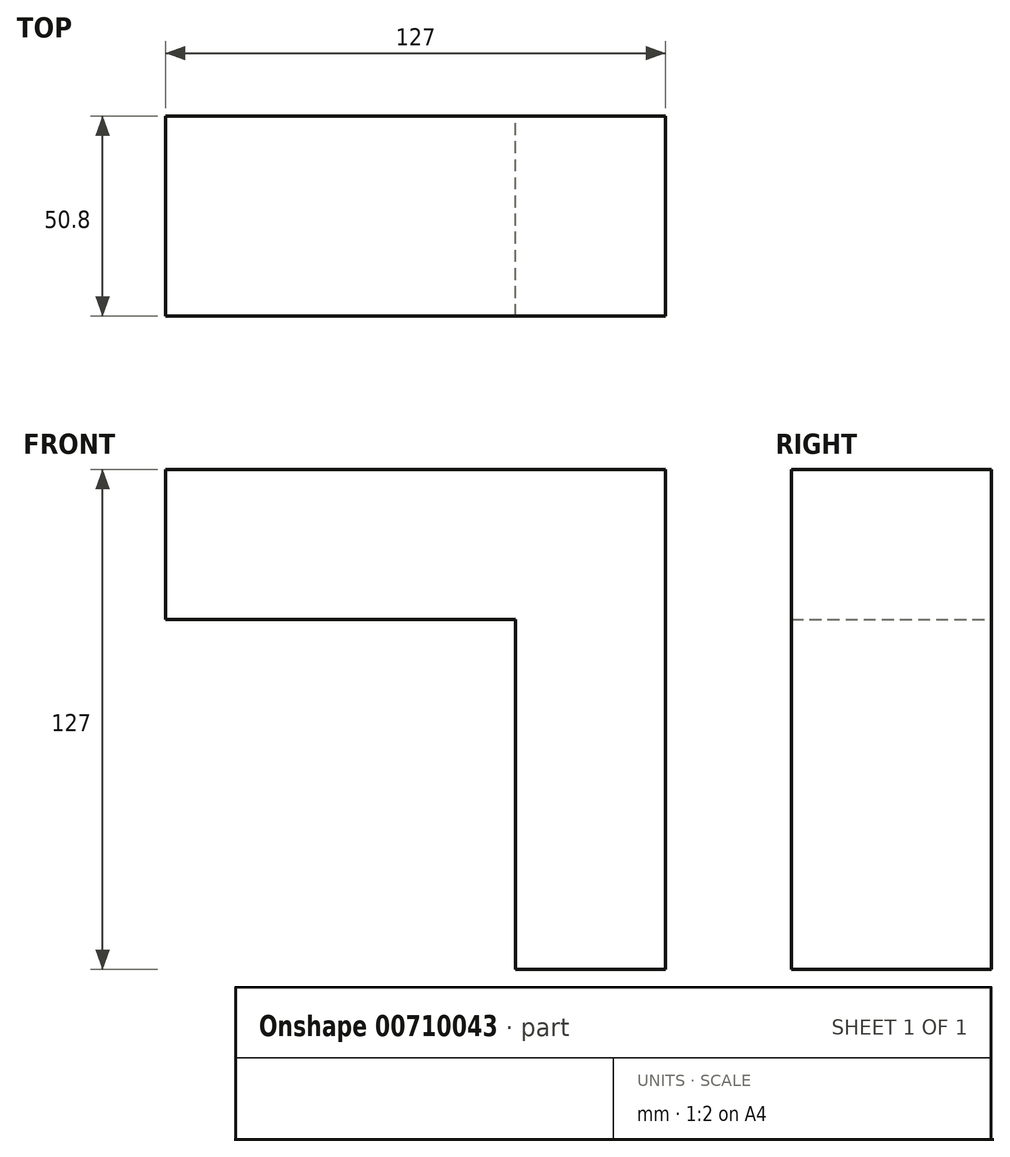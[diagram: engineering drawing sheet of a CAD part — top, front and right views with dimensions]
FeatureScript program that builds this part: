
annotation { "Feature Type Name" : "Feature", "Feature Type Description" : "" }
export const myFeature = defineFeature(function(context is Context, id is Id, definition is map)
    precondition{}
    {
        {
            var Q0;
            Q0=qCreatedBy(makeId("Front.planeOp"),FACE);
            var sketch = newSketch(context, id + "F0", { "sketchPlane" : qUnion([Q0])});
            skLineSegment(sketch, "E0", {"start": v(0, 0) * mm, "end": v(192.92, 0) * mm, "construction": true});
            skLineSegment(sketch, "E1", {"start": v(127, 0) * mm, "end": v(127, 127) * mm});
            skLineSegment(sketch, "E2", {"start": v(127, 127) * mm, "end": v(0, 127) * mm});
            skLineSegment(sketch, "E3", {"start": v(0, 127) * mm, "end": v(0, 88.9) * mm});
            skLineSegment(sketch, "E4", {"start": v(0, 88.9) * mm, "end": v(88.9, 88.9) * mm});
            skLineSegment(sketch, "E5", {"start": v(88.9, 88.9) * mm, "end": v(88.9, 0) * mm});
            skLineSegment(sketch, "E6", {"start": v(127, 0) * mm, "end": v(88.9, 0) * mm});
            skSolve(sketch);
        }
        {
            var Q0;
            Q0 = qSketchRegion(id + "F0", true);
            extrude(context, id + "F1", {"entities" : qUnion([Q0]), "endBound" : BoundingType.SYMMETRIC, "depth" : 50.8 * mm, "offsetDistance" : 25.4 * mm});
        }
    });
